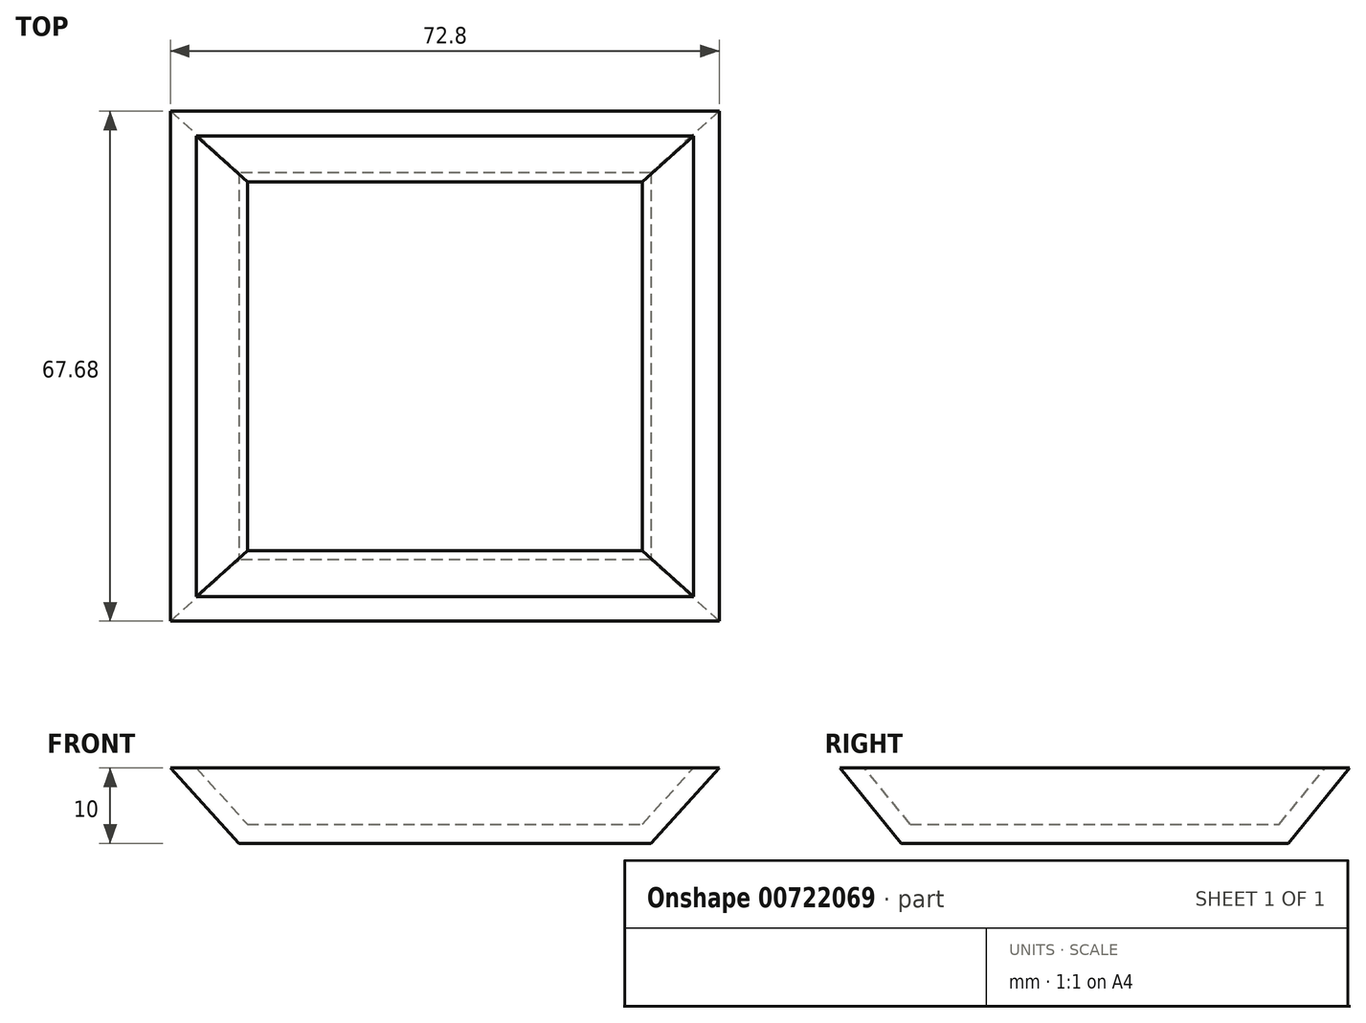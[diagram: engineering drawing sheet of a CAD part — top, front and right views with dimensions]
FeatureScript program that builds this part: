
annotation { "Feature Type Name" : "Feature", "Feature Type Description" : "" }
export const myFeature = defineFeature(function(context is Context, id is Id, definition is map)
    precondition{}
    {
        {
            var Q0;
            Q0=qCreatedBy(makeId("Top.planeOp"),FACE);
            var sketch = newSketch(context, id + "F0", { "sketchPlane" : qUnion([Q0])});
            skLineSegment(sketch, "E0.bottom", {"start": v(27.33, 25.7) * mm, "end": v(-27.33, 25.7) * mm});
            skLineSegment(sketch, "E0.top", {"start": v(27.33, -25.7) * mm, "end": v(-27.33, -25.7) * mm});
            skLineSegment(sketch, "E0.left", {"start": v(27.33, 25.7) * mm, "end": v(27.33, -25.7) * mm});
            skLineSegment(sketch, "E0.right", {"start": v(-27.33, 25.7) * mm, "end": v(-27.33, -25.7) * mm});
            skPoint(sketch, "E0.middle", {"position": v(0, 0) * mm});
            skSolve(sketch);
        }
        {
            var Q0;
            Q0=makeQuery(id+"F0.imprint","IMPRINT",FACE,{"disambiguationData":[TD([[makeQuery(id+"F0.imprint","IMPRINT",EDGE,{"derivedFrom":sQuery(id+"F0.wireOp",EDGE,"E0.bottom")}),1.0]])]});
            extrude(context, id + "F1", {"entities" : qUnion([Q0]), "depth" : 2 * mm, "offsetDistance" : 25.4 * mm});
        }
        {
            var Q0;
            Q0=qCreatedBy(makeId("Top.planeOp"),FACE);
            cPlane(context, id + "F2", {"entities" : qUnion([Q0]), "cplaneType" : CPlaneType.OFFSET, "offset" : 10 * mm, "width" : 152.4 * mm, "height" : 152.4 * mm});
        }
        {
            var Q0;
            Q0=qCreatedBy(id+"F2.planeOp",FACE);
            var sketch = newSketch(context, id + "F3", { "sketchPlane" : qUnion([Q0])});
            skLineSegment(sketch, "E1.bottom", {"start": v(36.4, 33.84) * mm, "end": v(-36.4, 33.84) * mm});
            skLineSegment(sketch, "E1.top", {"start": v(36.4, -33.84) * mm, "end": v(-36.4, -33.84) * mm});
            skLineSegment(sketch, "E1.left", {"start": v(36.4, 33.84) * mm, "end": v(36.4, -33.84) * mm});
            skLineSegment(sketch, "E1.right", {"start": v(-36.4, 33.84) * mm, "end": v(-36.4, -33.84) * mm});
            skPoint(sketch, "E1.middle", {"position": v(0, 0) * mm});
            skSolve(sketch);
        }
        {
            var Q1;
            Q1=makeQuery(id+"F3.imprint","IMPRINT",FACE,{"disambiguationData":[TD([[makeQuery(id+"F3.imprint","IMPRINT",EDGE,{"derivedFrom":sQuery(id+"F3.wireOp",EDGE,"E1.bottom")}),1.0]])]});
            var Q2;
            Q2=makeQuery(id+"F1.opExtrude","CAP_FACE",FACE,{"disambiguationData":[OSD([sQuery(id+"F0.wireOp",EDGE,"E0.bottom"),sQuery(id+"F0.wireOp",EDGE,"E0.top"),sQuery(id+"F0.wireOp",EDGE,"E0.left"),sQuery(id+"F0.wireOp",EDGE,"E0.right")])],"isStart":true});
            loft(context, id + "F4", {"operationType" : NewBodyOperationType.ADD, "sheetProfilesArray" : [{ "sheetProfileEntities" : qUnion([Q1]) }, { "sheetProfileEntities" : qUnion([Q2]) }]});
        }
        {
            var Q0;
            Q0=makeQuery(id+"F4.opLoft","CAP_FACE",FACE,{"disambiguationData":[OSD([makeQuery(id+"F3.imprint","IMPRINT",FACE,{"disambiguationData":[TD([[makeQuery(id+"F3.imprint","IMPRINT",EDGE,{"derivedFrom":sQuery(id+"F3.wireOp",EDGE,"E1.bottom")}),1.0]])]})])],"isStart":true});
            shell(context, id + "F5", {"entities" : qUnion([Q0]), "thickness" : 2.54 * mm});
        }
        {
            var Q0;
            Q0=qCreatedBy(makeId("Front.planeOp"),FACE);
            var sketch = newSketch(context, id + "F6", { "sketchPlane" : qUnion([Q0])});
            skLineSegment(sketch, "E2", {"start": v(-47.33, -15.47) * mm, "end": v(44.77, -30.12) * mm});
            skSolve(sketch);
        }
        {
            var Q0;
            Q0=qCreatedBy(makeId("Front.planeOp"),FACE);
            var Q1;
            Q1=sQuery(id+"F6.wireOp",EDGE,"E2");
            cPlane(context, id + "F7", {"entities" : qUnion([Q0, Q1]), "cplaneType" : CPlaneType.LINE_ANGLE, "offset" : 3 * mm, "angle" : 10 * degree, "width" : 152.4 * mm, "height" : 152.4 * mm});
        }
        {
            var Q0;
            Q0=qCreatedBy(id+"F7.planeOp",FACE);
            var sketch = newSketch(context, id + "F8", { "sketchPlane" : qUnion([Q0])});
            skLineSegment(sketch, "E3", {"start": v(-44.9, -48.72) * mm, "end": v(45.54, -48.72) * mm});
            skLineSegment(sketch, "E4", {"start": v(-44.9, -48.72) * mm, "end": v(-44.9, -29.67) * mm});
            skLineSegment(sketch, "E5", {"start": v(45.54, -48.72) * mm, "end": v(47.24, -15.24) * mm});
            skSolve(sketch);
        }
        {
            var Q0;
            Q0=sQuery(id+"F8.wireOp",EDGE,"E3");
            cPlane(context, id + "F9", {"entities" : qUnion([Q0]), "cplaneType" : CPlaneType.LINE_ANGLE, "offset" : 25.4 * mm, "angle" : 90 * degree, "width" : 152.4 * mm, "height" : 152.4 * mm});
        }
        {
            var Q0;
            Q0=qCreatedBy(id+"F9.planeOp",FACE);
            var sketch = newSketch(context, id + "F10", { "sketchPlane" : qUnion([Q0])});
            skFitSpline(sketch, "E6", {"points": [v(-45.4, 5.7) * mm, v(-18, 0.9) * mm, v(9.78, 6.4) * mm, v(45, 3.26) * mm], "startDerivative": vector(87.2, -25.1) * mm, "endDerivative": vector(101.04, -18.42) * mm});
            skSolve(sketch);
        }
        {
            var Q0;
            Q0=sQuery(id+"F8.wireOp",EDGE,"E5");
            var Q1;
            Q1=sQuery(id+"F8.wireOp",EDGE,"E4");
            var Q2;
            Q2=sQuery(id+"F10.wireOp",EDGE,"E6");
            loft(context, id + "F11", {"bodyType" : ToolBodyType.SURFACE, "addGuides" : true, "wireProfilesArray" : [{ "wireProfileEntities" : qUnion([Q0]) }, { "wireProfileEntities" : qUnion([Q1]) }], "guidesArray" : [{ "guideEntities" : qUnion([Q2]), "guideDerivativeType" : LoftGuideDerivativeType.DEFAULT, "guideDerivativeMagnitude" : 1 }]});
        }
    });
